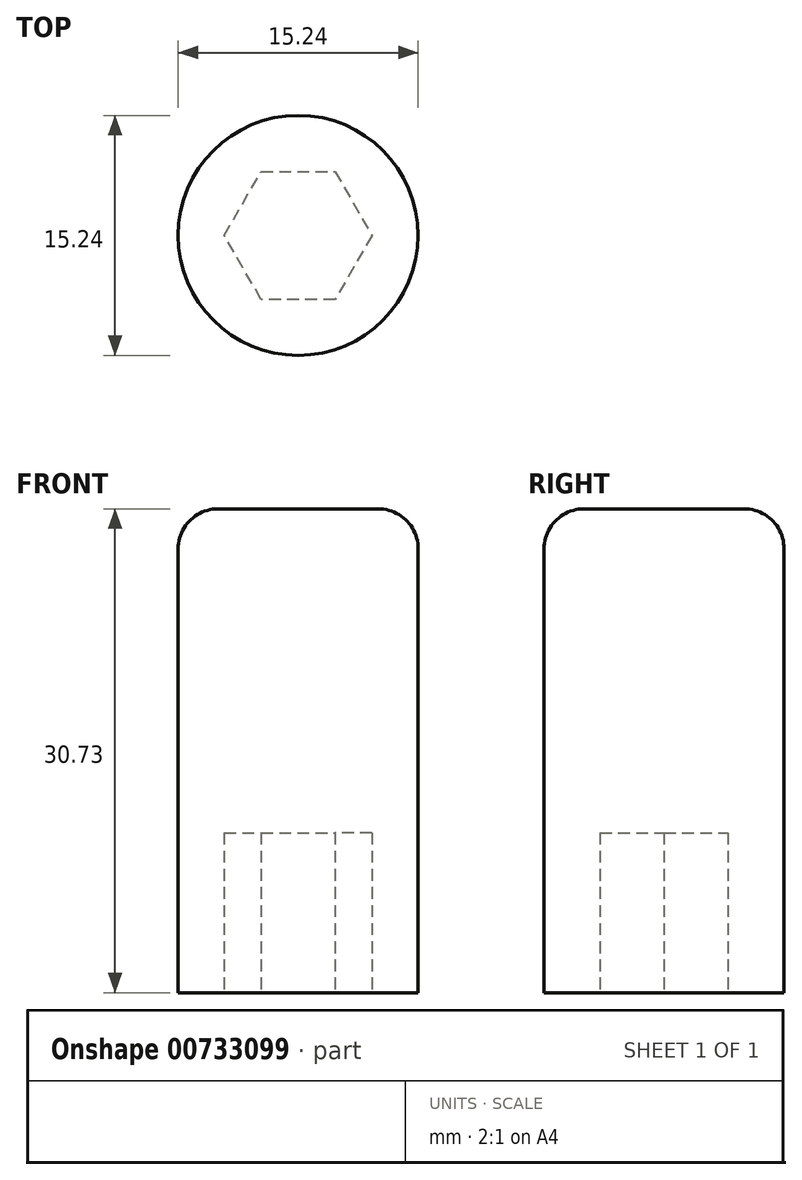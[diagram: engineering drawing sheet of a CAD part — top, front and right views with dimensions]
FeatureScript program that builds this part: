
annotation { "Feature Type Name" : "Feature", "Feature Type Description" : "" }
export const myFeature = defineFeature(function(context is Context, id is Id, definition is map)
    precondition{}
    {
        {
            var Q0;
            Q0=qCreatedBy(makeId("Top.planeOp"),FACE);
            var sketch = newSketch(context, id + "F0", { "sketchPlane" : qUnion([Q0])});
            skCircle(sketch, "E0", {"center": v(0, 0) * mm, "radius": 7.62 * mm});
            skSolve(sketch);
        }
        {
            var Q0;
            Q0 = qSketchRegion(id + "F0", true);
            extrude(context, id + "F1", {"entities" : qUnion([Q0]), "depth" : 30.73 * mm, "offsetDistance" : 25.4 * mm});
        }
        {
            var Q0;
            Q0=makeQuery(id+"F1.opExtrude","CAP_EDGE",EDGE,{"disambiguationData":[OSD([sQuery(id+"F0.wireOp",EDGE,"E0")])],"isStart":false});
            fillet(context, id + "F2", {"entities" : qUnion([Q0]), "radius" : 2.54 * mm, "tangentPropagation" : true, "allowEdgeOverflow" : false});
        }
        {
            var Q0;
            Q0=qCreatedBy(makeId("Top.planeOp"),FACE);
            var sketch = newSketch(context, id + "F3", { "sketchPlane" : qUnion([Q0])});
            skCircle(sketch, "E1.cCircle", {"center": v(0, 0) * mm, "radius": 4.06 * mm, "construction": true});
            skLineSegment(sketch, "E1.0", {"start": v(-2.35, 4.06) * mm, "end": v(2.35, 4.06) * mm});
            skLineSegment(sketch, "E1.1", {"start": v(2.35, 4.06) * mm, "end": v(4.7, 0) * mm});
            skLineSegment(sketch, "E1.2", {"start": v(4.7, 0) * mm, "end": v(2.35, -4.06) * mm});
            skLineSegment(sketch, "E1.3", {"start": v(2.35, -4.06) * mm, "end": v(-2.35, -4.06) * mm});
            skLineSegment(sketch, "E1.4", {"start": v(-2.35, -4.06) * mm, "end": v(-4.7, 0) * mm});
            skLineSegment(sketch, "E1.5", {"start": v(-4.7, 0) * mm, "end": v(-2.35, 4.06) * mm});
            skPoint(sketch, "E1.0.midPoint", {"position": v(0, 4.06) * mm});
            skSolve(sketch);
        }
        {
            var Q0;
            Q0 = qSketchRegion(id + "F3", true);
            extrude(context, id + "F4", {"entities" : qUnion([Q0]), "operationType" : NewBodyOperationType.REMOVE, "depth" : 10.16 * mm, "offsetDistance" : 25.4 * mm});
        }
    });
